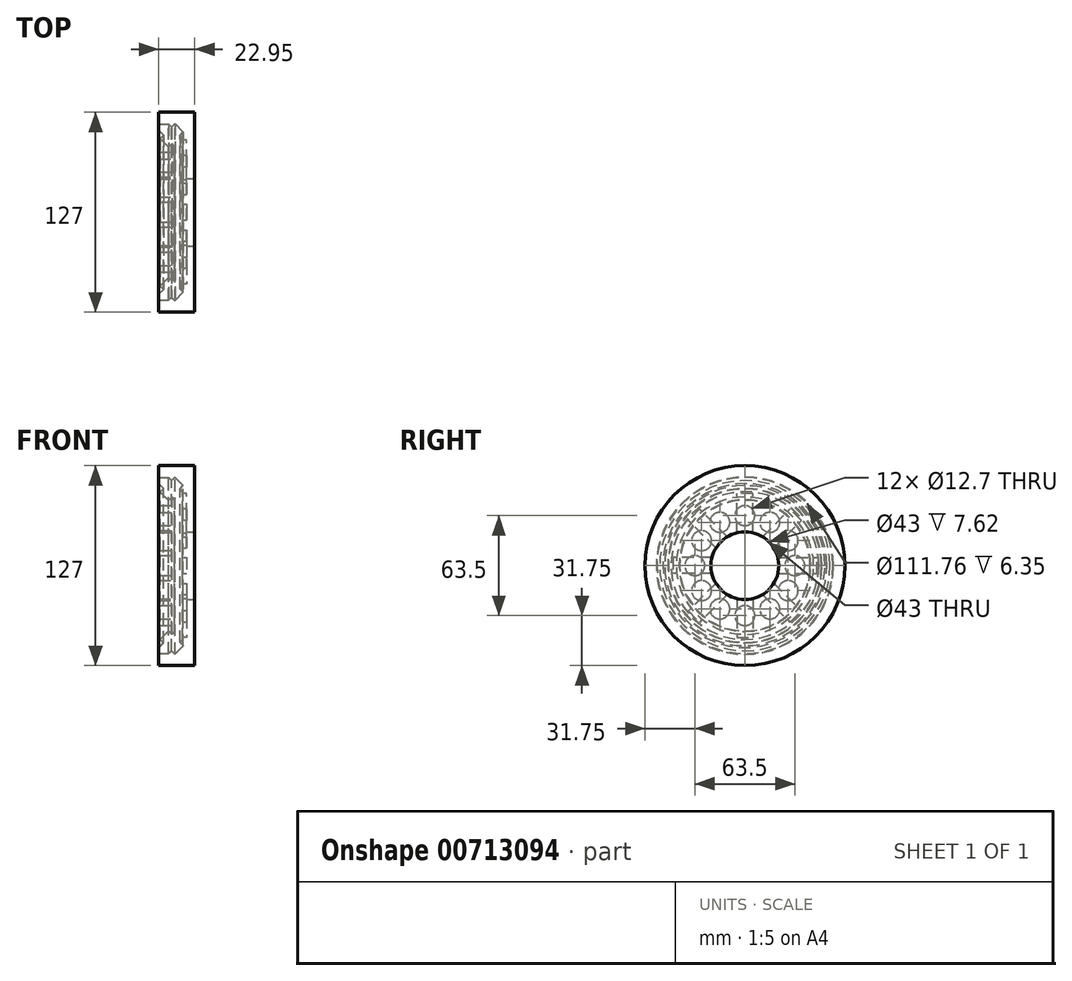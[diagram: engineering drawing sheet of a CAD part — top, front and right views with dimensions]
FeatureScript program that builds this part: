
annotation { "Feature Type Name" : "Feature", "Feature Type Description" : "" }
export const myFeature = defineFeature(function(context is Context, id is Id, definition is map)
    precondition{}
    {
        {
            var Q0;
            Q0=qCreatedBy(makeId("Front.planeOp"),FACE);
            var sketch = newSketch(context, id + "F0", { "sketchPlane" : qUnion([Q0])});
            skLineSegment(sketch, "E0", {"start": v(-22.95, 0) * mm, "end": v(22.95, 0) * mm});
            skLineSegment(sketch, "E1", {"start": v(22.95, 0) * mm, "end": v(22.95, 42) * mm});
            skLineSegment(sketch, "E2", {"start": v(22.95, 42) * mm, "end": v(15.33, 42) * mm});
            skLineSegment(sketch, "E3", {"start": v(15.33, 42) * mm, "end": v(15.33, 16.6) * mm});
            skLineSegment(sketch, "E4", {"start": v(15.33, 16.6) * mm, "end": v(6.35, 7.62) * mm});
            skLineSegment(sketch, "E5", {"start": v(6.35, 7.62) * mm, "end": v(-6.35, 7.62) * mm});
            skLineSegment(sketch, "E6", {"start": v(-6.35, 7.62) * mm, "end": v(-15.33, 16.6) * mm});
            skLineSegment(sketch, "E7", {"start": v(-15.33, 16.6) * mm, "end": v(-15.33, 42) * mm});
            skLineSegment(sketch, "E8", {"start": v(-15.33, 42) * mm, "end": v(-22.95, 42) * mm});
            skLineSegment(sketch, "E9", {"start": v(-22.95, 42) * mm, "end": v(-22.95, 0) * mm});
            skLineSegment(sketch, "E10", {"start": v(0, 11.43) * mm, "end": v(-10.25, 21.68) * mm});
            skLineSegment(sketch, "E11", {"start": v(-10.25, 21.68) * mm, "end": v(-10.25, 42) * mm});
            skLineSegment(sketch, "E12", {"start": v(-10.25, 42) * mm, "end": v(10.25, 42) * mm});
            skLineSegment(sketch, "E13", {"start": v(10.25, 42) * mm, "end": v(10.25, 21.68) * mm});
            skLineSegment(sketch, "E14", {"start": v(10.25, 21.68) * mm, "end": v(0, 11.43) * mm});
            skLineSegment(sketch, "E15", {"start": v(0, 11.43) * mm, "end": v(0, 42) * mm});
            skLineSegment(sketch, "E16", {"start": v(0, 7.62) * mm, "end": v(0, 0) * mm});
            skLineSegment(sketch, "E17", {"start": v(8.45, 19.88) * mm, "end": v(6.3, 22.04) * mm});
            skLineSegment(sketch, "E18", {"start": v(6.3, 22.04) * mm, "end": v(0.91, 16.65) * mm});
            skLineSegment(sketch, "E19", {"start": v(0.91, 16.65) * mm, "end": v(3.07, 14.5) * mm});
            skLineSegment(sketch, "E20", {"start": v(8.15, 9.42) * mm, "end": v(10.3, 7.26) * mm});
            skLineSegment(sketch, "E21", {"start": v(10.3, 7.26) * mm, "end": v(15.69, 12.65) * mm});
            skLineSegment(sketch, "E22", {"start": v(15.69, 12.65) * mm, "end": v(13.53, 14.8) * mm});
            skSolve(sketch);
        }
        {
            var Q0;
            Q0=qCreatedBy(makeId("Front.planeOp"),FACE);
            var sketch = newSketch(context, id + "F1", { "sketchPlane" : qUnion([Q0])});
            skLineSegment(sketch, "E23", {"start": v(20.16, 63.5) * mm, "end": v(-23.6, 63.5) * mm});
            skSolve(sketch);
        }
        {
            var Q0;
            {var subQ7=sQuery(id+"F0.wireOp",EDGE,"E1");Q0=makeQuery(id+"F0.imprint","IMPRINT",FACE,{"disambiguationData":[TD([[makeQuery(id+"F0.imprint","IMPRINT",EDGE,{"derivedFrom":subQ7}),1.0]])]});}
            var Q1;
            {var subQ3=sQuery(id+"F0.wireOp",EDGE,"E13");Q1=makeQuery(id+"F0.imprint","IMPRINT",FACE,{"disambiguationData":[TD([[makeQuery(id+"F0.imprint","IMPRINT",EDGE,{"derivedFrom":subQ3}),-1.0]])]});}
            var Q2;
            Q2=sQuery(id+"F1.wireOp",EDGE,"E23");
            revolve(context, id + "F2", {"surfaceOperationType" : NewSurfaceOperationType.NEW, "entities" : qUnion([Q0, Q1]), "axis" : qUnion([Q2]), "revolveType" : RevolveType.FULL});
        }
        {
            var Q0;
            Q0=makeQuery(id+"F2.opRevolve","SWEPT_FACE",FACE,{"disambiguationData":[OSD([sQuery(id+"F0.wireOp",EDGE,"E13")])]});
            var sketch = newSketch(context, id + "F3", { "sketchPlane" : qUnion([Q0])});
            skCircle(sketch, "E24", {"center": v(0, 31.75) * mm, "radius": 6.35 * mm});
            skPoint(sketch, "E25.center", {"position": v(0, 0) * mm});
            skCircle(sketch, "E26.1.0", {"center": v(15.87, 36) * mm, "radius": 6.35 * mm});
            skCircle(sketch, "E26.2.0", {"center": v(27.5, 47.62) * mm, "radius": 6.35 * mm});
            skCircle(sketch, "E26.3.0", {"center": v(31.75, 63.5) * mm, "radius": 6.35 * mm});
            skCircle(sketch, "E26.4.0", {"center": v(27.5, 79.38) * mm, "radius": 6.35 * mm});
            skCircle(sketch, "E26.5.0", {"center": v(15.87, 91) * mm, "radius": 6.35 * mm});
            skCircle(sketch, "E26.6.0", {"center": v(0, 95.25) * mm, "radius": 6.35 * mm});
            skCircle(sketch, "E26.7.0", {"center": v(-15.87, 91) * mm, "radius": 6.35 * mm});
            skCircle(sketch, "E26.8.0", {"center": v(-27.5, 79.38) * mm, "radius": 6.35 * mm});
            skCircle(sketch, "E26.9.0", {"center": v(-31.75, 63.5) * mm, "radius": 6.35 * mm});
            skCircle(sketch, "E26.10.0", {"center": v(-27.5, 47.62) * mm, "radius": 6.35 * mm});
            skCircle(sketch, "E26.11.0", {"center": v(-15.88, 36) * mm, "radius": 6.35 * mm});
            skPoint(sketch, "E26.center", {"position": v(0, 63.5) * mm});
            skSolve(sketch);
        }
        {
            var Q0;
            Q0 = qSketchRegion(id + "F3", true);
            extrude(context, id + "F4", {"entities" : qUnion([Q0]), "operationType" : NewBodyOperationType.REMOVE, "oppositeDirection" : true, "depth" : 25.4 * mm, "offsetDistance" : 25.4 * mm});
        }
        {
            var Q0;
            Q0=makeQuery(id+"F2.opRevolve","SWEPT_FACE",FACE,{"disambiguationData":[OSD([sQuery(id+"F0.wireOp",EDGE,"E3")])]});
            var sketch = newSketch(context, id + "F5", { "sketchPlane" : qUnion([Q0])});
            skLineSegment(sketch, "E27.bottom", {"start": v(5.08, 45.72) * mm, "end": v(-5.08, 45.72) * mm});
            skLineSegment(sketch, "E27.top", {"start": v(5.08, 17.78) * mm, "end": v(-5.08, 17.78) * mm});
            skLineSegment(sketch, "E27.left", {"start": v(5.08, 45.72) * mm, "end": v(5.08, 17.78) * mm});
            skLineSegment(sketch, "E27.right", {"start": v(-5.08, 45.72) * mm, "end": v(-5.08, 17.78) * mm});
            skPoint(sketch, "E27.middle", {"position": v(0, 31.75) * mm});
            skLineSegment(sketch, "E28.1.0", {"start": v(8.98, 47.34) * mm, "end": v(28.74, 27.58) * mm});
            skLineSegment(sketch, "E28.1.1", {"start": v(16.16, 54.52) * mm, "end": v(8.98, 47.34) * mm});
            skLineSegment(sketch, "E28.1.2", {"start": v(16.16, 54.52) * mm, "end": v(35.92, 34.76) * mm});
            skLineSegment(sketch, "E28.1.3", {"start": v(35.92, 34.76) * mm, "end": v(28.74, 27.58) * mm});
            skLineSegment(sketch, "E28.2.0", {"start": v(17.78, 58.42) * mm, "end": v(45.72, 58.42) * mm});
            skLineSegment(sketch, "E28.2.1", {"start": v(17.78, 68.58) * mm, "end": v(17.78, 58.42) * mm});
            skLineSegment(sketch, "E28.2.2", {"start": v(17.78, 68.58) * mm, "end": v(45.72, 68.58) * mm});
            skLineSegment(sketch, "E28.2.3", {"start": v(45.72, 68.58) * mm, "end": v(45.72, 58.42) * mm});
            skLineSegment(sketch, "E28.3.0", {"start": v(16.16, 72.48) * mm, "end": v(35.92, 92.24) * mm});
            skLineSegment(sketch, "E28.3.1", {"start": v(8.98, 79.66) * mm, "end": v(16.16, 72.48) * mm});
            skLineSegment(sketch, "E28.3.2", {"start": v(8.98, 79.66) * mm, "end": v(28.74, 99.42) * mm});
            skLineSegment(sketch, "E28.3.3", {"start": v(28.74, 99.42) * mm, "end": v(35.92, 92.24) * mm});
            skLineSegment(sketch, "E28.4.0", {"start": v(5.08, 81.28) * mm, "end": v(5.08, 109.22) * mm});
            skLineSegment(sketch, "E28.4.1", {"start": v(-5.08, 81.28) * mm, "end": v(5.08, 81.28) * mm});
            skLineSegment(sketch, "E28.4.2", {"start": v(-5.08, 81.28) * mm, "end": v(-5.08, 109.22) * mm});
            skLineSegment(sketch, "E28.4.3", {"start": v(-5.08, 109.22) * mm, "end": v(5.08, 109.22) * mm});
            skLineSegment(sketch, "E28.5.0", {"start": v(-8.98, 79.66) * mm, "end": v(-28.74, 99.42) * mm});
            skLineSegment(sketch, "E28.5.1", {"start": v(-16.16, 72.48) * mm, "end": v(-8.98, 79.66) * mm});
            skLineSegment(sketch, "E28.5.2", {"start": v(-16.16, 72.48) * mm, "end": v(-35.92, 92.24) * mm});
            skLineSegment(sketch, "E28.5.3", {"start": v(-35.92, 92.24) * mm, "end": v(-28.74, 99.42) * mm});
            skLineSegment(sketch, "E28.6.0", {"start": v(-17.78, 68.58) * mm, "end": v(-45.72, 68.58) * mm});
            skLineSegment(sketch, "E28.6.1", {"start": v(-17.78, 58.42) * mm, "end": v(-17.78, 68.58) * mm});
            skLineSegment(sketch, "E28.6.2", {"start": v(-17.78, 58.42) * mm, "end": v(-45.72, 58.42) * mm});
            skLineSegment(sketch, "E28.6.3", {"start": v(-45.72, 58.42) * mm, "end": v(-45.72, 68.58) * mm});
            skLineSegment(sketch, "E28.7.0", {"start": v(-16.16, 54.52) * mm, "end": v(-35.92, 34.76) * mm});
            skLineSegment(sketch, "E28.7.1", {"start": v(-8.98, 47.34) * mm, "end": v(-16.16, 54.52) * mm});
            skLineSegment(sketch, "E28.7.2", {"start": v(-8.98, 47.34) * mm, "end": v(-28.74, 27.58) * mm});
            skLineSegment(sketch, "E28.7.3", {"start": v(-28.74, 27.58) * mm, "end": v(-35.92, 34.76) * mm});
            skPoint(sketch, "E28.center", {"position": v(0, 63.5) * mm});
            skSolve(sketch);
        }
        {
            var Q0;
            Q0 = qSketchRegion(id + "F5", true);
            extrude(context, id + "F6", {"entities" : qUnion([Q0]), "operationType" : NewBodyOperationType.REMOVE, "oppositeDirection" : true, "depth" : 2.54 * mm, "offsetDistance" : 25.4 * mm});
        }
    });
